# Revit family: Building-IEC309Connections-GEWISS-IEC309BTS-90°_SURF_MOUNT_INLET_20-25V_IP44
name_source: partatom
category: Apparecchi elettrici
units: mm (PartAtom-declared; Revit-internal decimal feet)

## family parameters
Condiviso = No
Host = Superficie
Mantenere orientamento annotazione = Sì
Punto di calcolo locali = Sì
Quota connettore circolare = Usa diametro
Taglio con vuoti quando caricato = No
Tipo di parte = Normale

## types (18) — shared parameters
BLOCCO = B=C
Catalogue = BUILDING
Corpo centrale = Default(2)
Electrocod = 2230
FORMULA = 1000 mm  [stored 3.28084 ft]
Glow wire test: = 850 °C (active parts) - 650 °C (passive parts)
IDF = 296db634-9b8b-4885-b434-385580f18e3b
IDT = 821e2a5f66e94c3ca955b7df865af73c
IP degree = IP44
Immagine tipo = <Nessuno>
Insulation resistance = - 10 M?
L = 155 mm
Operating temperature: = -25 +40 °C
Piastra = Default(2)
Produttore = GEWISS S.p.A.
Prospetto di default = 1219 mm
SEO = Inlet
SPinotto = Default(2)
Shock resistance = IK08
Spostamento_S = 955 mm
Technical sheet = https://www.gewiss.com
Thermo-pressure with ball = 125 °C (active parts) - 80 °C (passive parts)
Type of wiring = With screw
Typology = 90° angled surface mounting inlet
URL = https://www.gewiss.com
Version file RFA = 21.11
W = 115 mm

## per-type parameters (varying)
| type | Breaking capacity at 1.1 Un | Colour: | Descrizione | Frequency | Modello | No. of poles | Permissible overload | Rated current (A) | Rated voltage: | Reference h: | Terminal tightening capacity | Total number of operations |
| GW60470 - IP44 90°APPL.INLET 2P 16A 24/42V 11H | 20A | Green | IP44 90°APPL.INLET 2P 16A 24/42V 11H | 401 - 500 Hz | GW60470 | 2P | 22A | 16 | 20-25V and 40-50 V | 11 | 1-2.5mm² flexible cables - 1.5-4mm² rigid cables | -5000 |
| GW60473 - IP44 90°APPL.INLET 2P 32A 24V N.R. | 40A | Violet | IP44 90°APPL.INLET 2P 32A 24V N.R. | 50 - 60 Hz | GW60473 | 2P | 42A | 32 | 20-25 V | - | 2.5-6mm² flexible cables - 2.5-10mm² rigid cables | -2000 |
| GW60464 - IP44 90°APPL.INLET 2P 16A 24V N.R. | 20A | Violet | IP44 90°APPL.INLET 2P 16A 24V N.R. | 50 - 60 Hz | GW60464 | 2P | 22A | 16 | 20-25 V | - | 1-2.5mm² flexible cables - 1.5-4mm² rigid cables | -5000 |
| GW60467 - IP44 90°APPL.INLET 3P 16A 42V 12H | 20A | White | IP44 90°APPL.INLET 3P 16A 42V 12H | 50 - 60 Hz | GW60467 | 3P | 22A | 16 | 40-50 V | 12 | 1-2.5mm² flexible cables - 1.5-4mm² rigid cables | -5000 |
| GW60474 - IP44 90°APPL.INLET 3P 32A 24V N.R. | 40A | Violet | IP44 90°APPL.INLET 3P 32A 24V N.R. | 50 - 60 Hz | GW60474 | 3P | 42A | 32 | 20-25 V | - | 2.5-6mm² flexible cables - 2.5-10mm² rigid cables | -2000 |
| GW60478 - IP44 90°APPL.INLET 3P 32A 24/42V 4H | 40A | Green | IP44 90°APPL.INLET 3P 32A 24/42V 4H | 100 - 200 Hz | GW60478 | 3P | 42A | 32 | 20-25V and 40-50 V | 4 | 2.5-6mm² flexible cables - 2.5-10mm² rigid cables | -2000 |
| GW60471 - IP44 90°APPL.INLET 3P 16A 24/42V 11H | 20A | Green | IP44 90°APPL.INLET 3P 16A 24/42V 11H | 401 - 500 Hz | GW60471 | 3P | 22A | 16 | 20-25V and 40-50 V | 11 | 1-2.5mm² flexible cables - 1.5-4mm² rigid cables | -5000 |
| GW60480 - IP44 90°APPL.INLET 3P 32A 24/42V 11H | 40A | Green | IP44 90°APPL.INLET 3P 32A 24/42V 11H | 401 - 500 Hz | GW60480 | 3P | 42A | 32 | 20-25V and 40-50 V | 11 | 2.5-6mm² flexible cables - 2.5-10mm² rigid cables | -2000 |
| GW60469 - IP44 90°APPL.INLET 3P 16A 24/42V 4H | 20A | Green | IP44 90°APPL.INLET 3P 16A 24/42V 4H | 100 - 200 Hz | GW60469 | 3P | 22A | 16 | 20-25V and 40-50 V | 4 | 1-2.5mm² flexible cables - 1.5-4mm² rigid cables | -5000 |
| GW60466 - IP44 90°APPL.INLET 2P 16A 42V 12H | 20A | White | IP44 90°APPL.INLET 2P 16A 42V 12H | 50 - 60 Hz | GW60466 | 2P | 22A | 16 | 40-50 V | 12 | 1-2.5mm² flexible cables - 1.5-4mm² rigid cables | -5000 |
| GW60479 - IP44 90°APPL.INLET 2P 32A 24/42V 11H | 40A | Green | IP44 90°APPL.INLET 2P 32A 24/42V 11H | 401 - 500 Hz | GW60479 | 2P | 42A | 32 | 20-25V and 40-50 V | 11 | 2.5-6mm² flexible cables - 2.5-10mm² rigid cables | -2000 |
| GW60472 - IP44 90°APPL.INLET 2P 16A CC 24/42V 10H | 20A | White | IP44 90°APPL.INLET 2P 16A CC 24/42V 10H | d.c. | GW60472 | 2P | 22A | 16 | 20-25V and 40-50 V | 10 | 1-2.5mm² flexible cables - 1.5-4mm² rigid cables | -5000 |
| GW60481 - IP44 90°APPL.INLET 2P 32A CC 24/42V 10H | 40A | White | IP44 90°APPL.INLET 2P 32A CC 24/42V 10H | d.c. | GW60481 | 2P | 42A | 32 | 20-25V and 40-50 V | 10 | 2.5-6mm² flexible cables - 2.5-10mm² rigid cables | -2000 |
| GW60476 - IP44 90°APPL.INLET 3P 32A 42V 12H | 40A | White | IP44 90°APPL.INLET 3P 32A 42V 12H | 50 - 60 Hz | GW60476 | 3P | 42A | 32 | 40-50 V | 12 | 2.5-6mm² flexible cables - 2.5-10mm² rigid cables | -2000 |
| GW60477 - IP44 90°APPL.INLET 2P 32A 24/42V 4H | 40A | Green | IP44 90°APPL.INLET 2P 32A 24/42V 4H | 100 - 200 Hz | GW60477 | 2P | 42A | 32 | 20-25V and 40-50 V | 4 | 2.5-6mm² flexible cables - 2.5-10mm² rigid cables | -2000 |
| GW60468 - IP44 90°APPL.INLET 2P 16A 24/42V 4H | 20A | Green | IP44 90°APPL.INLET 2P 16A 24/42V 4H | 100 - 200 Hz | GW60468 | 2P | 22A | 16 | 20-25V and 40-50 V | 4 | 1-2.5mm² flexible cables - 1.5-4mm² rigid cables | -5000 |
| GW60475 - IP44 90°APPL.INLET 2P 32A 42V 12H | 40A | White | IP44 90°APPL.INLET 2P 32A 42V 12H | 50 - 60 Hz | GW60475 | 2P | 42A | 32 | 40-50 V | 12 | 2.5-6mm² flexible cables - 2.5-10mm² rigid cables | -2000 |
| GW60465 - IP44 90°APPL.INLET 3P 16A 24V N.R. | 20A | Violet | IP44 90°APPL.INLET 3P 16A 24V N.R. | 50 - 60 Hz | GW60465 | 3P | 22A | 16 | 20-25 V | - | 1-2.5mm² flexible cables - 1.5-4mm² rigid cables | -5000 |

note: [stored X ft] marks values corroborated as IEEE doubles in the binary element streams (Revit-internal decimal feet)

## geometry (parser evidence)
native form markers: Sweep x2
no freeform markers — native parametric forms only
